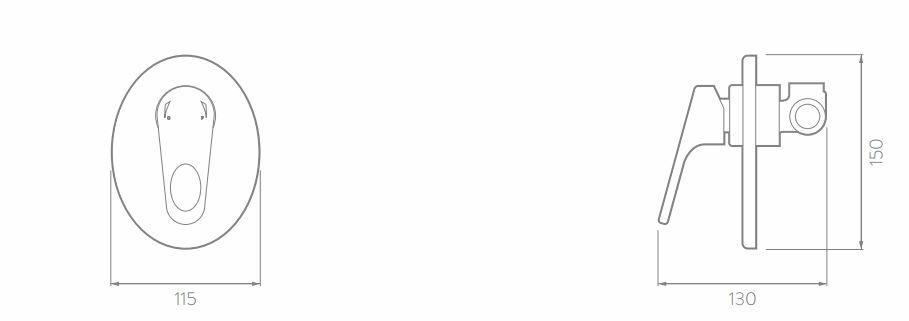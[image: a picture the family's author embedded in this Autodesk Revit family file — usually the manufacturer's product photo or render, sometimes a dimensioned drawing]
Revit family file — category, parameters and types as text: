
# Revit family: KR4085551_Ducha Monocontrol Koral PRO Mate Black
name_source: partatom
category: Plumbing Fixtures
units: mm (PartAtom-declared; Revit-internal decimal feet)

## family parameters
Always vertical = Yes
Cut with Voids When Loaded = No
Host = Wall
OmniClass Number = 23.45.05.14.17
Part Type = Normal
Room Calculation Point = No
Round Connector Dimension = Use Diameter
Shared = No

## types (2) — shared parameters
Alto = 946 mm
Altura ducha = 2000 mm  [stored 6.56168 ft]
Altura mezclador = 1200 mm
Ancho = 152 mm
Capacidad de flujo = 80 psi: 9,3 L/min
Fabricante = Corona
Garantía = 30 años
Peso neto = 1.200 g. - 2,60 lb
Presion maxima = 125 psi (860 kPa)
Presion minima = 20 psi (140 kPa)
Profundidad = 329 mm  [stored 1.0794 ft]
Referencia = KR4085551
Temperatura de uso = 5˚C a 71˚C
URL = https://corona.co

## per-type parameters (varying)
| type | Material |
| Acabado Cromado | Corona_Cromado |
| Acabado X | Corona_Mate_Black |

note: [stored X ft] marks values corroborated as IEEE doubles in the binary element streams (Revit-internal decimal feet)

## geometry (parser evidence)
native form markers: Sweep x10
no freeform markers — native parametric forms only
